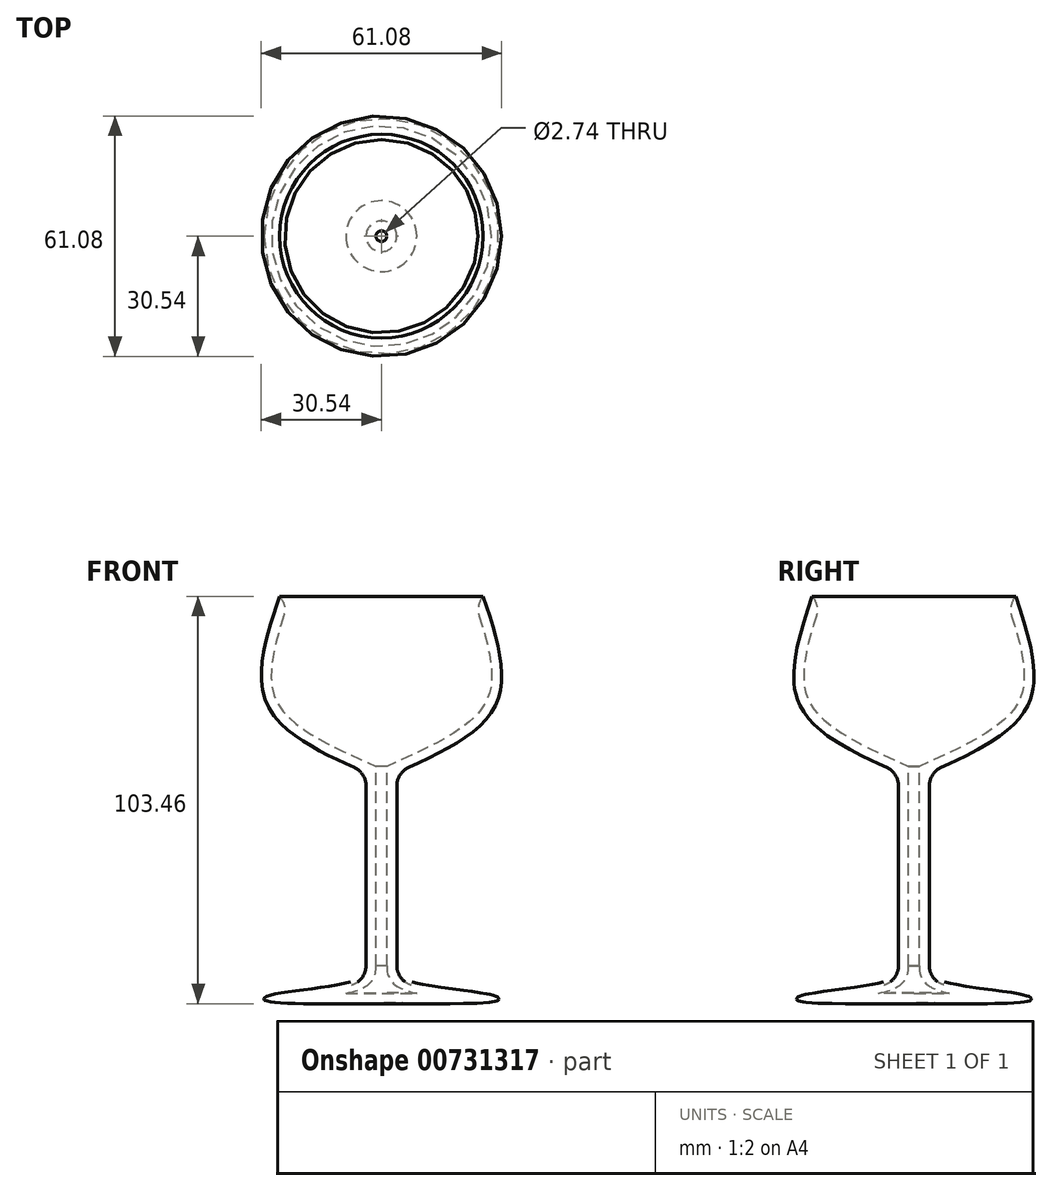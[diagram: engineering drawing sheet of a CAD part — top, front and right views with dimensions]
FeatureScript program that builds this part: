
annotation { "Feature Type Name" : "Feature", "Feature Type Description" : "" }
export const myFeature = defineFeature(function(context is Context, id is Id, definition is map)
    precondition{}
    {
        {
            var Q0;
            Q0=qCreatedBy(makeId("Front.planeOp"),FACE);
            var sketch = newSketch(context, id + "F0", { "sketchPlane" : qUnion([Q0])});
            skLineSegment(sketch, "E0", {"start": v(0, 27.22) * mm, "end": v(-25.87, 27.22) * mm});
            skFitSpline(sketch, "E1", {"points": [v(-25.87, 27.22) * mm, v(-29.18, 0) * mm, v(-3.91, -17.6) * mm], "startDerivative": vector(-20.4, -61.37) * mm, "endDerivative": vector(63.5, -28.58) * mm});
            skLineSegment(sketch, "E2", {"start": v(-3.91, -17.6) * mm, "end": v(-3.91, -66.62) * mm});
            skFitSpline(sketch, "E3", {"points": [v(-3.91, -66.62) * mm, v(-5.6, -69.84) * mm, v(-28.5, -74.17) * mm, v(-29.76, -75.25) * mm, v(0, -75.97) * mm], "startDerivative": vector(-0.51, -24.52) * mm, "endDerivative": vector(105.52, 2.27) * mm});
            skLineSegment(sketch, "E4", {"start": v(0, 27.22) * mm, "end": v(0, -75.97) * mm});
            skSolve(sketch);
        }
        {
            var Q0;
            {var subQ0=sQuery(id+"F0.wireOp",EDGE,"E0");Q0=makeQuery(id+"F0.imprint","IMPRINT",FACE,{"disambiguationData":[TD([[makeQuery(id+"F0.imprint","IMPRINT",EDGE,{"derivedFrom":subQ0}),1.0]])]});}
            var Q1;
            Q1=makeQuery(id+"F0.imprint","IMPRINT",FACE,{"disambiguationData":[TD([[makeQuery(id+"F0.imprint","IMPRINT",EDGE,{"derivedFrom":sQuery(id+"F0.wireOp",EDGE,"E2")}),1.0]])]});
            var Q2;
            Q2=sQuery(id+"F0.wireOp",EDGE,"E4");
            revolve(context, id + "F1", {"surfaceOperationType" : NewSurfaceOperationType.NEW, "entities" : qUnion([Q0, Q1]), "axis" : qUnion([Q2]), "revolveType" : RevolveType.FULL});
        }
        {
            var Q0;
            Q0=makeQuery(id+"F1.opRevolve","SWEPT_FACE",FACE,{"disambiguationData":[OSD([sQuery(id+"F0.wireOp",EDGE,"E0")])]});
            shell(context, id + "F2", {"entities" : qUnion([Q0]), "thickness" : 2.54 * mm});
        }
        {
            var Q0;
            Q0=makeQuery(id+"F1.opRevolve","SWEPT_EDGE",EDGE,{"disambiguationData":[OSD([sQuery(id+"F0.wireOp",EDGE,"E1"),sQuery(id+"F0.wireOp",EDGE,"E2"),sQuery(id+"F0.wireOp",EDGE,"sx51uN7G-xGL2-Qym7-6PHx-r0CNKGvKvhS2")])]});
            var Q1;
            Q1=makeQuery(id+"F1.opRevolve","SWEPT_EDGE",EDGE,{"disambiguationData":[OSD([sQuery(id+"F0.wireOp",EDGE,"E2"),sQuery(id+"F0.wireOp",EDGE,"E3")])]});
            var Q2;
            Q2=makeQuery(id+"F1.opRevolve","SWEPT_FACE",FACE,{"disambiguationData":[OSD([sQuery(id+"F0.wireOp",EDGE,"E3")])]});
            var Q3;
            Q3=makeQuery(id+"F2.opShell","OFFSET_EDGE",EDGE,{"disambiguationData":[OSD([sQuery(id+"F0.wireOp",EDGE,"E0"),sQuery(id+"F0.wireOp",EDGE,"E1")])]});
            fillet(context, id + "F3", {"entities" : qUnion([Q0, Q1, Q2, Q3]), "radius" : 5.08 * mm, "allowEdgeOverflow" : false});
        }
    });
